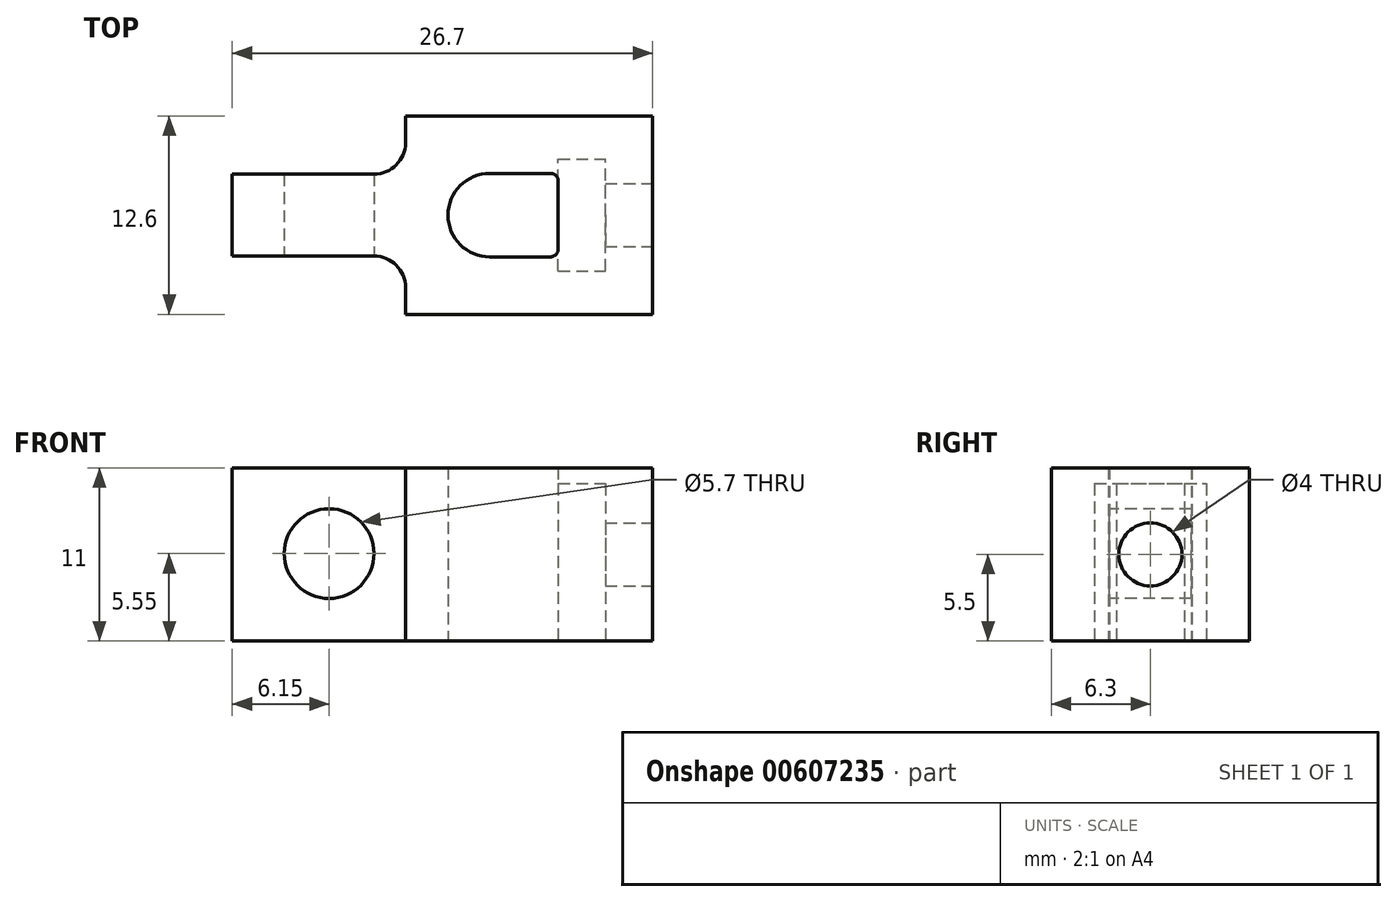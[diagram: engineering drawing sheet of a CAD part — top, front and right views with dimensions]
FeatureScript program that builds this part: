
annotation { "Feature Type Name" : "Feature", "Feature Type Description" : "" }
export const myFeature = defineFeature(function(context is Context, id is Id, definition is map)
    precondition{}
    {
        {
            var Q0;
            Q0=qCreatedBy(makeId("Top.planeOp"),FACE);
            var sketch = newSketch(context, id + "F0", { "sketchPlane" : qUnion([Q0])});
            skLineSegment(sketch, "E0", {"start": v(-15.7, 0) * mm, "end": v(0, 0) * mm});
            skLineSegment(sketch, "E1", {"start": v(0, 0) * mm, "end": v(0, 12.6) * mm});
            skLineSegment(sketch, "E2", {"start": v(0, 12.6) * mm, "end": v(-15.7, 12.6) * mm});
            skLineSegment(sketch, "E3", {"start": v(-15.7, 12.6) * mm, "end": v(-15.7, 10.9) * mm});
            skLineSegment(sketch, "E4", {"start": v(-17.7, 8.9) * mm, "end": v(-26.7, 8.9) * mm});
            skLineSegment(sketch, "E5", {"start": v(-26.7, 8.9) * mm, "end": v(-26.7, 3.7) * mm});
            skLineSegment(sketch, "E6", {"start": v(-26.7, 3.7) * mm, "end": v(-17.7, 3.7) * mm});
            skLineSegment(sketch, "E7", {"start": v(-15.7, 1.7) * mm, "end": v(-15.7, 0) * mm});
            skPoint(sketch, "E8.visualSharp", {"position": v(-15.7, 8.9) * mm});
            skArc(sketch, "E8.filletArc", {"start": v(-17.7, 8.9) * mm, "mid": v(-16.29, 9.49) * mm, "end": v(-15.7, 10.9) * mm});
            skPoint(sketch, "E9.visualSharp", {"position": v(-15.7, 3.7) * mm});
            skArc(sketch, "E9.filletArc", {"start": v(-15.7, 1.7) * mm, "mid": v(-16.29, 3.11) * mm, "end": v(-17.7, 3.7) * mm});
            skLineSegment(sketch, "E10", {"start": v(-6.5, 3.65) * mm, "end": v(-10.35, 3.65) * mm});
            skLineSegment(sketch, "E11", {"start": v(-6.5, 8.95) * mm, "end": v(-10.35, 8.95) * mm});
            skArc(sketch, "E12", {"start": v(-10.35, 8.95) * mm, "mid": v(-13, 6.3) * mm, "end": v(-10.35, 3.65) * mm});
            skLineSegment(sketch, "E13", {"start": v(-10.35, 8.95) * mm, "end": v(-10.35, 6.3) * mm, "construction": true});
            skLineSegment(sketch, "E14", {"start": v(-10.35, 6.3) * mm, "end": v(-10.35, 3.65) * mm, "construction": true});
            skLineSegment(sketch, "E15", {"start": v(-6, 4.15) * mm, "end": v(-6, 8.45) * mm});
            skPoint(sketch, "E16.visualSharp", {"position": v(-6, 3.65) * mm});
            skArc(sketch, "E16.filletArc", {"start": v(-6.5, 3.65) * mm, "mid": v(-6.15, 3.8) * mm, "end": v(-6, 4.15) * mm});
            skPoint(sketch, "E17.visualSharp", {"position": v(-6, 8.95) * mm});
            skArc(sketch, "E17.filletArc", {"start": v(-6, 8.45) * mm, "mid": v(-6.15, 8.8) * mm, "end": v(-6.5, 8.95) * mm});
            skSolve(sketch);
        }
        {
            var Q0;
            Q0=makeQuery(id+"F0.imprint","IMPRINT",FACE,{"disambiguationData":[TD([[makeQuery(id+"F0.imprint","IMPRINT",EDGE,{"derivedFrom":sQuery(id+"F0.wireOp",EDGE,"E0")}),1.0]])]});
            extrude(context, id + "F1", {"entities" : qUnion([Q0]), "depth" : 11 * mm, "offsetDistance" : 25 * mm});
        }
        {
            var Q0;
            Q0=makeQuery(id+"F1.opExtrude","SWEPT_FACE",FACE,{"disambiguationData":[OSD([sQuery(id+"F0.wireOp",EDGE,"E6")])]});
            var sketch = newSketch(context, id + "F2", { "sketchPlane" : qUnion([Q0])});
            skCircle(sketch, "E18", {"center": v(-20.55, 5.55) * mm, "radius": 2.85 * mm});
            skSolve(sketch);
        }
        {
            var Q0;
            Q0=makeQuery(id+"F2.imprint","IMPRINT",FACE,{"disambiguationData":[TD([[makeQuery(id+"F2.imprint","IMPRINT",EDGE,{"derivedFrom":sQuery(id+"F2.wireOp",EDGE,"E18")}),1.0]])]});
            extrude(context, id + "F3", {"entities" : qUnion([Q0]), "operationType" : NewBodyOperationType.REMOVE, "oppositeDirection" : true, "depth" : 25 * mm, "offsetDistance" : 25 * mm});
        }
        {
            var Q0;
            Q0=makeQuery(id+"F1.opExtrude","CAP_FACE",FACE,{"disambiguationData":[OSD([sQuery(id+"F0.wireOp",EDGE,"E0"),sQuery(id+"F0.wireOp",EDGE,"E1"),sQuery(id+"F0.wireOp",EDGE,"E2"),sQuery(id+"F0.wireOp",EDGE,"E3"),sQuery(id+"F0.wireOp",EDGE,"E4"),sQuery(id+"F0.wireOp",EDGE,"E5"),sQuery(id+"F0.wireOp",EDGE,"E6"),sQuery(id+"F0.wireOp",EDGE,"E7"),sQuery(id+"F0.wireOp",EDGE,"E8.filletArc"),sQuery(id+"F0.wireOp",EDGE,"E9.filletArc"),sQuery(id+"F0.wireOp",EDGE,"E10"),sQuery(id+"F0.wireOp",EDGE,"E11"),sQuery(id+"F0.wireOp",EDGE,"E12"),sQuery(id+"F0.wireOp",EDGE,"DLjIItnD-rDWE-uYbW-Kcuf-LAVMzs5vsyhz")])],"isStart":true});
            var sketch = newSketch(context, id + "F4", { "sketchPlane" : qUnion([Q0])});
            skLineSegment(sketch, "E19.bottom", {"start": v(-6, -2.75) * mm, "end": v(-3, -2.75) * mm});
            skLineSegment(sketch, "E19.top", {"start": v(-6, -9.85) * mm, "end": v(-3, -9.85) * mm});
            skLineSegment(sketch, "E19.left", {"start": v(-6, -2.75) * mm, "end": v(-6, -9.85) * mm});
            skLineSegment(sketch, "E19.right", {"start": v(-3, -2.75) * mm, "end": v(-3, -9.85) * mm});
            skSolve(sketch);
        }
        {
            var Q0;
            {var subQ3=sQuery(id+"F4.wireOp",EDGE,"E19.bottom");Q0=makeQuery(id+"F4.imprint","IMPRINT",FACE,{"disambiguationData":[TD([[makeQuery(id+"F4.imprint","IMPRINT",EDGE,{"derivedFrom":subQ3}),-1.0]])]});}
            extrude(context, id + "F5", {"entities" : qUnion([Q0]), "operationType" : NewBodyOperationType.REMOVE, "oppositeDirection" : true, "depth" : 10 * mm, "offsetDistance" : 25 * mm});
        }
        {
            var Q0;
            Q0=makeQuery(id+"F1.opExtrude","SWEPT_FACE",FACE,{"disambiguationData":[OSD([sQuery(id+"F0.wireOp",EDGE,"E1")])]});
            var sketch = newSketch(context, id + "F6", { "sketchPlane" : qUnion([Q0])});
            skCircle(sketch, "E20", {"center": v(6.3, 5.5) * mm, "radius": 2 * mm});
            skLineSegment(sketch, "E21", {"start": v(6.3, 0) * mm, "end": v(6.3, 5.5) * mm, "construction": true});
            skLineSegment(sketch, "E22", {"start": v(0, 5.5) * mm, "end": v(6.3, 5.5) * mm, "construction": true});
            skSolve(sketch);
        }
        {
            var Q0;
            Q0=makeQuery(id+"F6.imprint","IMPRINT",FACE,{"disambiguationData":[TD([[makeQuery(id+"F6.imprint","IMPRINT",EDGE,{"derivedFrom":sQuery(id+"F6.wireOp",EDGE,"E20")}),1.0]])]});
            extrude(context, id + "F7", {"entities" : qUnion([Q0]), "operationType" : NewBodyOperationType.REMOVE, "endBound" : BoundingType.UP_TO_NEXT, "oppositeDirection" : true, "depth" : 25 * mm, "offsetDistance" : 25 * mm});
        }
    });
